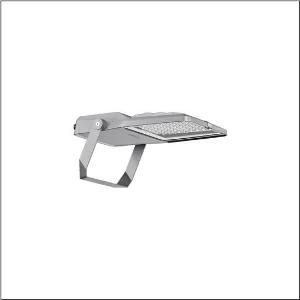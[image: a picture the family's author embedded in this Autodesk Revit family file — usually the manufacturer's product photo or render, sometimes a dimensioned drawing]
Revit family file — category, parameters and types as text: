
# Revit family: floodlight_fl_21_iq_mini___pl33t_5xa7771d4f1a_3e9c
name_source: partatom
category: Lighting Fixtures
units: mm (PartAtom-declared; Revit-internal decimal feet)

## family parameters
Cut with Voids When Loaded = No
Host = Face
Light Source = No
Part Type = Normal
Room Calculation Point = No
Round Connector Dimension = Use Diameter
Shared = No

## types (1)
- --- (1 x LED, 18390 lm, 143 W, 4000K)
    Apparent Load = 143 VA
    CIE Flux Codes = 26 75 99 100 100
    Color Rendering = 70
    Color Temperature = 4000K
    Default Elevation = 1800 mm
    Description = Floodlight FL 21 iQ mini, floodlight, primary light control with lens, of PMMA, primary optical cover: protective disc, of toughened safety glass, transparent, light distribution: PL33T, light emission: direct distribution, installation type: surface-mounted, LED, High Power LED, rated luminous flux: 18.390lm, luminous efficacy: 129lm/W, light colour: 740, colour temperature: 4000K, control: Auto-Match, Temp-Guard, Lumen-Switch, Night-Set, Smart-Wire, Light-Fading, Desk-Remote (wireless, voltage-free reading and setting of iQ features in the workshop via application-optimized NFC function/RFID function), optimised constant luminous flux control (CLO 2.0), with terminal, 6-pole, mains connection: 220..240V, AC, 50/60Hz, start of lifetime: 143W, end of service life: 152W, reduction: 61W, luminaire housing, of diecast aluminium, powder-coated, Siteco® metallic grey (DB 702S), corrosivity category C5 mid according to DIN EN ISO 12944, sealing non-destructively replaceable, mounting bracket, of steel, galvanised, powder-coated, Siteco® metallic grey (DB 702S), protection rating (complete): IP66, insulation class (complete): insulation class II (safety insulation), certification: CE, ENEC, VDE, protection symbol: D, impact resistance: IK08, permissible operating ambient temperature: -40..+40°C, permissible operating ambient temperature for outdoor applications: -40..+50°C, standard: DIN EN 12944, LABS conformity tested according to VDMA 24364:2018-05, packaging unit: 1 piece

Light Distribution: PL33T
    Height = 70 mm
    Lamp = 1 x LED
    Lamp Light Flux = 18390 lm
    Lamp Power = 143 W
    Lamp count = 1
    Length = 485 mm
    Luminous efficacy = 129 lm/W
    Manufacturer = Siteco
    ModVariant = No
    Model = 5XA7771D4F1A
    Number of Poles = 1
    OnlyDefault = Yes
    Power Factor = 1
    Product Name = Floodlight FL 21 iQ mini | PL33T
    Product group = floodlight | pylon annexe
    ProductGroupID = 6200
    Protection Class = Protection class II
    Protection Degree = IP 66
    RLX_Detail_Level = 1
    RLX_Emergency_Light_Flux = 0 lm
    RLX_Emergency_Type = 0
    RLX_Emergency_Type_DB = No
    RlxData = <blob elided: 96285 chars, md5=3449ec40>
    Socket = socket
    Standby Power = 0 W
    System Light Flux = 18390 lm
    System Power = 143 W
    Type Comments = factory setting: luminous flux: 100 % | dim-lin: 254 | 730 mA
    Type Image = l_1006845.jpg
    URL = http://relux.com
    VarID = @adj_081643
    Voltage = 0 V
    Weight = 0.00 kg
    Width = 337 mm

## geometry (parser evidence)
native form markers: Blend x4, Sweep x12
no freeform markers — native parametric forms only
